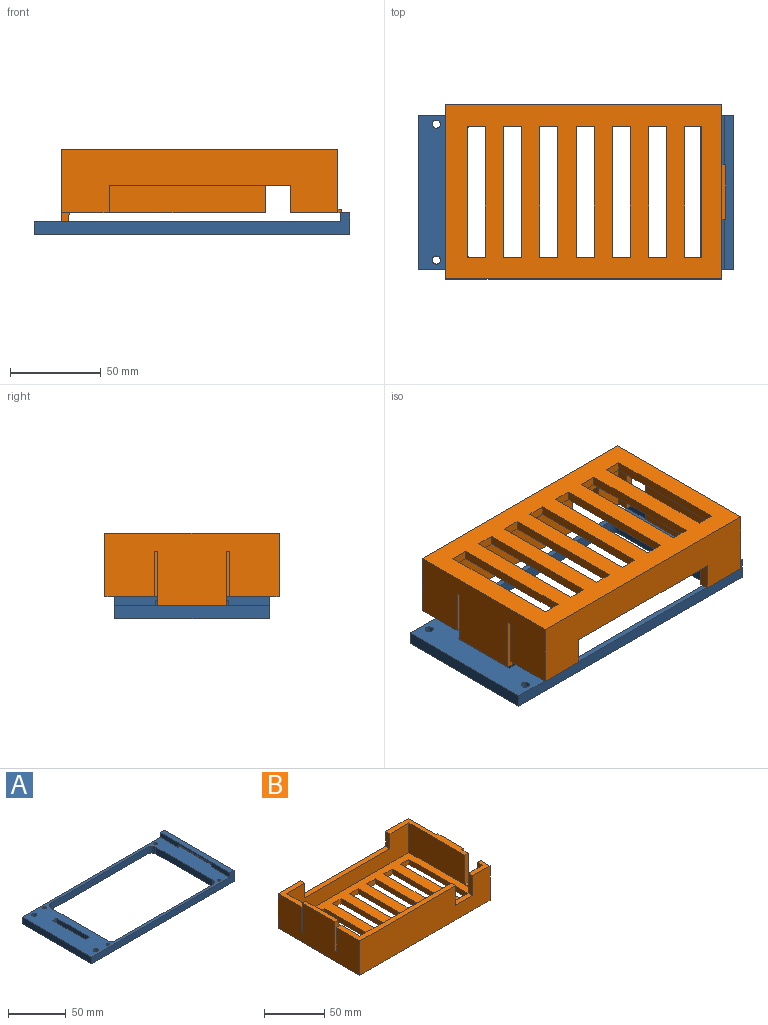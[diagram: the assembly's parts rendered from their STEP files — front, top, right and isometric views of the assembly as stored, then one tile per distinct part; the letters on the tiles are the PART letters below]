
ASSEMBLY  parts=2 mates=1
PART A: 30 faces, bbox 174x85x12 mm
  f0: plane 85x5mm, normal (-1,0,0), area 305mm2, adj f5,f12,f14,f17,f18,f19,f20
  f1: plane 40x7mm, normal (-1,0,0), area 280mm2, adj f2,f9,f14,f15
  f2: plane 7x5mm, normal (0,1,0), area 35mm2, adj f1,f3,f14,f15
  f3: plane 40x7mm, normal (1,0,0), area 280mm2, adj f2,f9,f14,f15
  f4: plane 85x7mm, normal (-1,0,0), area 595mm2, adj f5,f12,f14,f15
  f5: plane 174x12mm, normal (0,-1,0), area 1243mm2, adj f0,f4,f14,f15,f16,f17
  f6: cylinder r=1.45mm len=7mm, axis (0,0,-1), area 63.8mm2, adj f14,f15
  f7: cylinder r=2.25mm len=7mm, axis (0,0,-1), area 99mm2, adj f14,f15
  f8: cylinder r=2.25mm len=7mm, axis (0,0,-1), area 99mm2, adj f14,f15
  f9: plane 7x5mm, normal (0,-1,0), area 35mm2, adj f1,f3,f14,f15
  f10: cylinder r=1.45mm len=7mm, axis (0,0,-1), area 63.8mm2, adj f14,f15
  f11: cylinder r=1.45mm len=7mm, axis (0,0,-1), area 63.8mm2, adj f14,f15
  f12: plane 174x12mm, normal (0,1,0), area 1243mm2, adj f0,f4,f14,f15,f16,f17
  f13: cylinder r=1.45mm len=7mm, axis (0,0,-1), area 63.8mm2, adj f14,f15
  f14: plane 171x85mm, normal (0,0,1), area 4071mm2, adj f0,f1,f2,f3,f4,f5,f6,f7
  f15: plane 174x85mm, normal (0,0,-1), area 4416mm2, adj f1,f2,f3,f4,f5,f6,f7,f8
  f16: plane 85x12mm, normal (1,0,0), area 1020mm2, adj f5,f12,f15,f17
  f17: plane 85x5mm, normal (0,0,1), area 425mm2, adj f0,f5,f12,f16
  f18: plane 3x2mm, normal (0,1,0), area 6mm2, adj f0,f14,f19,f21
  f19: plane 40x2mm, normal (0,0,-1), area 80mm2, adj f0,f18,f20,f21
  f20: plane 3x2mm, normal (0,-1,0), area 6mm2, adj f0,f14,f19,f21
  f21: plane 40x3mm, normal (-1,0,0), area 120mm2, adj f14,f18,f19,f20
  f22: plane 69x7mm, normal (1,0,0), area 483mm2, adj f14,f15,f26,f29
  f23: plane 118.32x7mm, normal (0,1,0), area 828.2mm2, adj f14,f15,f26,f27
  f24: plane 69x7mm, normal (-1,0,0), area 483mm2, adj f14,f15,f27,f28
  f25: plane 118.32x7mm, normal (0,-1,0), area 828.2mm2, adj f14,f15,f28,f29
  f26: cylinder r=5mm len=7mm, axis (0,0,-1), area 55mm2, adj f14,f15,f22,f23
  f27: cylinder r=5mm len=7mm, axis (0,0,1), area 55mm2, adj f14,f15,f23,f24
  f28: cylinder r=5mm len=7mm, axis (0,0,-1), area 55mm2, adj f14,f15,f24,f25
  f29: cylinder r=5mm len=7mm, axis (0,0,1), area 55mm2, adj f14,f15,f22,f25
PART B: 64 faces, bbox 154.5x96x40 mm
  f0: plane 20x11.16mm, normal (0,0,1), area 124.6mm2, adj f1,f8,f9,f12,f24,f63
  f1: plane 152.5x35mm, normal (0,-1,0), area 4937.5mm2, adj f0,f3,f4,f6,f8,f61,f62,f63
  f2: plane 143.5x86mm, normal (0,0,1), area 7337mm2, adj f5,f9,f11,f12,f33,f34,f35,f36
  f3: plane 152.5x96mm, normal (0,0,-1), area 9636mm2, adj f1,f6,f8,f13,f33,f34,f35,f36
  f4: plane 112.5x27.2mm, normal (0,0,1), area 673.5mm2, adj f1,f5,f6,f12,f28,f61
  f5: plane 86x30mm, normal (1,0,0), area 2480mm2, adj f2,f4,f7,f11,f12,f15,f17,f28
  f6: plane 96x40mm, normal (-1,0,0), area 3448mm2, adj f1,f3,f4,f7,f13,f14,f15,f17
  f7: plane 27.2x26.25mm, normal (0,0,1), area 242.3mm2, adj f5,f6,f11,f13,f26,f30
  f8: plane 96x35mm, normal (1,0,0), area 2880.4mm2, adj f0,f1,f3,f10,f13,f18,f19,f20
  f9: plane 86x30mm, normal (-1,0,0), area 2160.4mm2, adj f0,f2,f10,f11,f12,f22,f23,f24
  f10: plane 70.48x28.25mm, normal (0,0,1), area 453.2mm2, adj f8,f9,f11,f13,f18,f19,f21,f23
  f11: plane 143.5x30mm, normal (0,-1,0), area 2805mm2, adj f2,f5,f7,f9,f10,f25,f26,f27
  f12: plane 143.5x30mm, normal (0,1,0), area 3905mm2, adj f0,f2,f4,f5,f9,f61,f62,f63
  f13: plane 152.5x35mm, normal (0,1,0), area 3837.5mm2, adj f3,f6,f7,f8,f10,f25,f26,f27
  f14: plane 37.6x3.6mm, normal (0,0,1), area 135.4mm2, adj f6,f15,f16,f17
  f15: plane 30x5mm, normal (0,1,0), area 144.5mm2, adj f5,f6,f14,f16,f31,f32
  f16: plane 37.6x1.53mm, normal (1,0,0), area 57.5mm2, adj f14,f15,f17,f32
  f17: plane 30x5mm, normal (0,-1,0), area 144.5mm2, adj f5,f6,f14,f16,f29,f32
  f18: plane 2x2mm, normal (0,1,0), area 4mm2, adj f8,f10,f20,f21
  f19: plane 2x2mm, normal (0,-1,0), area 4mm2, adj f8,f10,f20,f21
  f20: plane 30x2mm, normal (0,0,-1), area 60mm2, adj f8,f18,f19,f21
  f21: plane 30x2mm, normal (1,0,0), area 60mm2, adj f10,f18,f19,f20
  f22: plane 14.36x4mm, normal (0,0,1), area 57.4mm2, adj f8,f9,f23,f24
  f23: plane 29.21x4mm, normal (0,-1,0), area 116.9mm2, adj f8,f9,f10,f22
  f24: plane 29.21x4mm, normal (0,1,0), area 116.9mm2, adj f0,f8,f9,f22
  f25: plane 15x5mm, normal (-1,0,0), area 75mm2, adj f10,f11,f13,f27
  f26: plane 15x5mm, normal (1,0,0), area 75mm2, adj f7,f11,f13,f27
  f27: plane 100x5mm, normal (0,0,1), area 500mm2, adj f11,f13,f25,f26
  f28: plane 25x5mm, normal (0,1,0), area 125mm2, adj f4,f5,f6,f29
  f29: plane 5x2mm, normal (0,0,1), area 10mm2, adj f5,f6,f17,f28
  f30: plane 25x5mm, normal (0,-1,0), area 125mm2, adj f5,f6,f7,f31
  f31: plane 5x2mm, normal (0,0,1), area 10mm2, adj f5,f6,f15,f30
  f32: cylinder r=5mm len=37.6mm, axis (0,1,0), area 144.2mm2, adj f5,f15,f16,f17
  f33: plane 9.5x5mm, normal (0,-1,0), area 47.5mm2, adj f2,f3,f34,f36
  f34: plane 72x5mm, normal (1,0,0), area 360mm2, adj f2,f3,f33,f35
  f35: plane 9.5x5mm, normal (0,1,0), area 47.5mm2, adj f2,f3,f34,f36
  f36: plane 72x5mm, normal (-1,0,0), area 360mm2, adj f2,f3,f33,f35
  f37: plane 72x5mm, normal (-1,0,0), area 360mm2, adj f2,f3,f38,f40
  f38: plane 10x5mm, normal (0,-1,0), area 50mm2, adj f2,f3,f37,f39
  f39: plane 72x5mm, normal (1,0,0), area 360mm2, adj f2,f3,f38,f40
  f40: plane 10x5mm, normal (0,1,0), area 50mm2, adj f2,f3,f37,f39
  f41: plane 72x5mm, normal (-1,0,0), area 360mm2, adj f2,f3,f42,f44
  f42: plane 10x5mm, normal (0,-1,0), area 50mm2, adj f2,f3,f41,f43
  f43: plane 72x5mm, normal (1,0,0), area 360mm2, adj f2,f3,f42,f44
  f44: plane 10x5mm, normal (0,1,0), area 50mm2, adj f2,f3,f41,f43
  f45: plane 72x5mm, normal (-1,0,0), area 360mm2, adj f2,f3,f46,f48
  f46: plane 10x5mm, normal (0,-1,0), area 50mm2, adj f2,f3,f45,f47
  f47: plane 72x5mm, normal (1,0,0), area 360mm2, adj f2,f3,f46,f48
  f48: plane 10x5mm, normal (0,1,0), area 50mm2, adj f2,f3,f45,f47
  f49: plane 72x5mm, normal (-1,0,0), area 360mm2, adj f2,f3,f50,f52
  f50: plane 10x5mm, normal (0,-1,0), area 50mm2, adj f2,f3,f49,f51
  f51: plane 72x5mm, normal (1,0,0), area 360mm2, adj f2,f3,f50,f52
  f52: plane 10x5mm, normal (0,1,0), area 50mm2, adj f2,f3,f49,f51
  f53: plane 72x5mm, normal (-1,0,0), area 360mm2, adj f2,f3,f54,f56
  f54: plane 10x5mm, normal (0,-1,0), area 50mm2, adj f2,f3,f53,f55
  f55: plane 72x5mm, normal (1,0,0), area 360mm2, adj f2,f3,f54,f56
  f56: plane 10x5mm, normal (0,1,0), area 50mm2, adj f2,f3,f53,f55
  f57: plane 72x5mm, normal (-1,0,0), area 360mm2, adj f2,f3,f58,f60
  f58: plane 10x5mm, normal (0,-1,0), area 50mm2, adj f2,f3,f57,f59
  f59: plane 72x5mm, normal (1,0,0), area 360mm2, adj f2,f3,f58,f60
  f60: plane 10x5mm, normal (0,1,0), area 50mm2, adj f2,f3,f57,f59
  f61: plane 20x5mm, normal (1,0,0), area 100mm2, adj f1,f4,f12,f62
  f62: plane 20x5mm, normal (0,0,1), area 100mm2, adj f1,f12,f61,f63
  f63: plane 20x5mm, normal (-1,0,0), area 100mm2, adj f0,f1,f12,f62
PLACE A t=(117.11,114.3,142.46)mm
PLACE B rot(axis=(1,0,0),180deg) t=(117.26,199.8,189.46)mm
MATE fastened B.f14 <-> A.f14  axis (0,0,-1) through (80.32,156.8,149.46)mm
